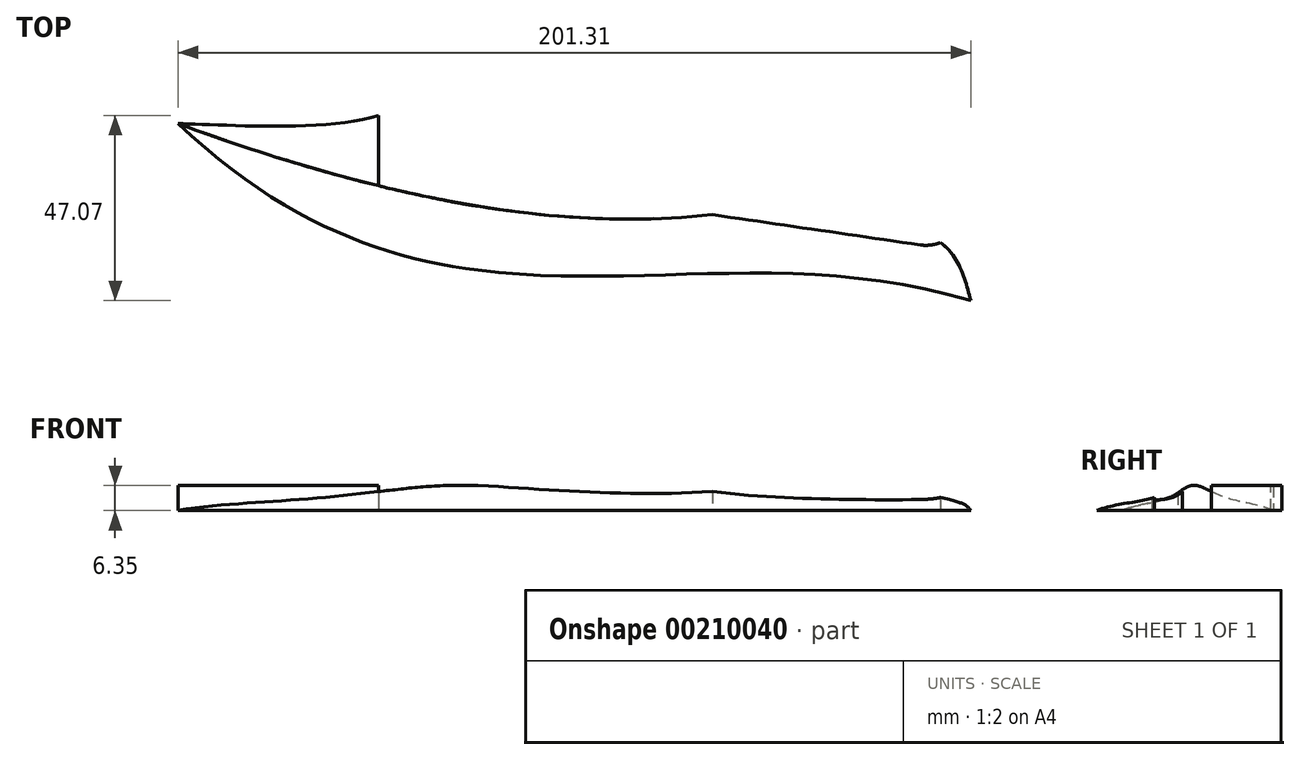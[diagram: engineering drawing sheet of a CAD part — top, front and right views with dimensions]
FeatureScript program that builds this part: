
annotation { "Feature Type Name" : "Feature", "Feature Type Description" : "" }
export const myFeature = defineFeature(function(context is Context, id is Id, definition is map)
    precondition{}
    {
        {
            var Q0;
            Q0=qCreatedBy(makeId("Top.planeOp"),FACE);
            var sketch = newSketch(context, id + "F0", { "sketchPlane" : qUnion([Q0])});
            skFitSpline(sketch, "E0", {"points": [v(0, 0) * mm, v(201.3, -44.96) * mm], "startDerivative": vector(205.46, -194.54) * mm, "endDerivative": vector(216.65, -64.43) * mm});
            skFitSpline(sketch, "E1", {"points": [v(201.3, -44.96) * mm, v(193.68, -30.23) * mm], "startDerivative": vector(-5.28, 22.16) * mm, "endDerivative": vector(-11.8, 8.9) * mm});
            skFitSpline(sketch, "E2", {"points": [v(0, 0) * mm, v(50.85, 2.11) * mm], "startDerivative": vector(25.64, 0) * mm, "endDerivative": vector(42.64, 13.77) * mm});
            skFitSpline(sketch, "E3", {"points": [v(50.85, 2.11) * mm, v(185, 0) * mm], "startDerivative": vector(165.72, -75.75) * mm, "endDerivative": vector(28.37, 18.67) * mm});
            skCircle(sketch, "E4", {"center": v(190, -20.76) * mm, "radius": 10.16 * mm});
            skFitSpline(sketch, "E5", {"points": [v(185, 0) * mm, v(183.03, -13.37) * mm], "startDerivative": vector(2.13, -12.58) * mm, "endDerivative": vector(-6.27, -13.9) * mm});
            skLineSegment(sketch, "E6", {"start": v(183.03, -13.37) * mm, "end": v(135.66, -23.13) * mm});
            skLineSegment(sketch, "E7", {"start": v(135.66, -23.13) * mm, "end": v(188.54, -30.81) * mm});
            skFitSpline(sketch, "E8", {"points": [v(0, 0) * mm, v(135.66, -23.13) * mm], "startDerivative": vector(221.55, -81.83) * mm, "endDerivative": vector(63.23, 6.44) * mm});
            skFitSpline(sketch, "E9", {"points": [v(50.85, 2.11) * mm, v(70.2, -19.94) * mm], "startDerivative": vector(14.46, -32.18) * mm, "endDerivative": vector(23.42, -10.45) * mm});
            skFitSpline(sketch, "E10", {"points": [v(185, 0) * mm, v(208.46, -9.9) * mm], "startDerivative": vector(40.59, -27.41) * mm, "endDerivative": vector(19.09, -3.05) * mm});
            skFitSpline(sketch, "E11", {"points": [v(208.46, -9.9) * mm, v(208.46, -24.03) * mm], "startDerivative": vector(0, -14.13) * mm, "endDerivative": vector(0, -14.13) * mm});
            skFitSpline(sketch, "E12", {"points": [v(208.46, -24.03) * mm, v(201.3, -44.96) * mm], "startDerivative": vector(-12.22, -16.03) * mm, "endDerivative": vector(5.28, -32.63) * mm});
            skFitSpline(sketch, "E13", {"points": [v(208.46, -9.9) * mm, v(250.55, -0.88) * mm], "startDerivative": vector(98.11, 0) * mm, "endDerivative": vector(54.56, 26.5) * mm});
            skFitSpline(sketch, "E14", {"points": [v(266.13, -17.4) * mm, v(237.98, -21.6) * mm], "startDerivative": vector(-21.76, -7.25) * mm, "endDerivative": vector(-59.94, -24.81) * mm});
            skFitSpline(sketch, "E15", {"points": [v(237.98, -21.6) * mm, v(208.46, -24.03) * mm], "startDerivative": vector(-29.01, -9.16) * mm, "endDerivative": vector(-16.03, -6.1) * mm});
            skFitSpline(sketch, "E16", {"points": [v(250.55, -0.88) * mm, v(266.13, -17.4) * mm], "startDerivative": vector(20, 2.63) * mm, "endDerivative": vector(-13.25, -57.76) * mm});
            skArc(sketch, "E17", {"start": v(179.84, -20.76) * mm, "mid": v(184.92, -25.84) * mm, "end": v(190, -20.76) * mm});
            skArc(sketch, "E18", {"start": v(200.16, -20.76) * mm, "mid": v(195.08, -15.68) * mm, "end": v(190, -20.76) * mm});
            skLineSegment(sketch, "E19", {"start": v(76.2, -20.98) * mm, "end": v(76.2, -37.25) * mm});
            skLineSegment(sketch, "E20", {"start": v(0, 0) * mm, "end": v(0, -58.13) * mm});
            skLineSegment(sketch, "E21", {"start": v(50.85, 2.11) * mm, "end": v(50.85, -15.78) * mm});
            skSolve(sketch);
        }
        {
            var Q0;
            Q0=makeQuery(id+"F0.imprint","IMPRINT",FACE,{"disambiguationData":[TD([[makeQuery(id+"F0.imprint","IMPRINT",EDGE,{"derivedFrom":sQuery(id+"F0.wireOp",EDGE,"E0")}),1.0]])]});
            extrude(context, id + "F1", {"entities" : qUnion([Q0]), "depth" : 6.35 * mm});
        }
        {
            var Q0;
            Q0=makeQuery(id+"F1.opExtrude","SWEPT_FACE",FACE,{"disambiguationData":[OSD([sQuery(id+"F0.wireOp",EDGE,"E19")])]});
            var sketch = newSketch(context, id + "F2", { "sketchPlane" : qUnion([Q0])});
            skLineSegment(sketch, "E22.bottom", {"start": v(-37.25, 0) * mm, "end": v(-20.98, 0) * mm});
            skLineSegment(sketch, "E22.top", {"start": v(-37.25, 6.35) * mm, "end": v(-20.98, 6.35) * mm});
            skLineSegment(sketch, "E22.left", {"start": v(-37.25, 0) * mm, "end": v(-37.25, 6.35) * mm});
            skLineSegment(sketch, "E22.right", {"start": v(-20.98, 0) * mm, "end": v(-20.98, 6.35) * mm});
            skFitSpline(sketch, "E23", {"points": [v(-37.25, 0) * mm, v(-20.98, 6.35) * mm], "startDerivative": vector(15.09, 7.25) * mm, "endDerivative": vector(7.36, 13.73) * mm});
            skSolve(sketch);
        }
        {
            var Q0;
            Q0=makeQuery(id+"F2.imprint","IMPRINT",FACE,{"disambiguationData":[TD([[makeQuery(id+"F2.imprint","IMPRINT",EDGE,{"derivedFrom":sQuery(id+"F2.wireOp",EDGE,"E22.top")}),1.0]])]});
            var Q1;
            Q1=makeQuery(id+"F1.opExtrude","CAP_EDGE",EDGE,{"disambiguationData":[OSD([sQuery(id+"F0.wireOp",EDGE,"E0")])],"isStart":true});
            sweep(context, id + "F3", {"operationType" : NewBodyOperationType.REMOVE, "profiles" : qUnion([Q0]), "path" : qUnion([Q1])});
        }
        {
            var Q0;
            {var subQ2=sQuery(id+"F0.wireOp",EDGE,"E1");Q0=makeQuery(id+"F0.imprint","IMPRINT",FACE,{"disambiguationData":[TD([[makeQuery(id+"F0.imprint","IMPRINT",EDGE,{"derivedFrom":subQ2}),1.0]])]});}
            extrude(context, id + "F4", {"entities" : qUnion([Q0]), "operationType" : NewBodyOperationType.ADD, "depth" : 6.35 * mm});
        }
        {
            var Q0;
            Q0=makeQuery(id+"F2.imprint","IMPRINT",FACE,{"disambiguationData":[TD([[makeQuery(id+"F2.imprint","IMPRINT",EDGE,{"derivedFrom":sQuery(id+"F2.wireOp",EDGE,"E22.top")}),1.0]])]});
            var Q1;
            Q1=makeQuery(id+"F4.opExtrude","CAP_EDGE",EDGE,{"disambiguationData":[OSD([sQuery(id+"F0.wireOp",EDGE,"E0")])],"isStart":false});
            sweep(context, id + "F5", {"operationType" : NewBodyOperationType.REMOVE, "profiles" : qUnion([Q0]), "path" : qUnion([Q1])});
        }
        {
            var Q0;
            {var subQ0=sQuery(id+"F0.wireOp",EDGE,"E2");Q0=makeQuery(id+"F0.imprint","IMPRINT",FACE,{"disambiguationData":[TD([[makeQuery(id+"F0.imprint","IMPRINT",EDGE,{"derivedFrom":subQ0}),-1.0]])]});}
            extrude(context, id + "F6", {"entities" : qUnion([Q0]), "operationType" : NewBodyOperationType.ADD, "depth" : 6.35 * mm});
        }
    });
